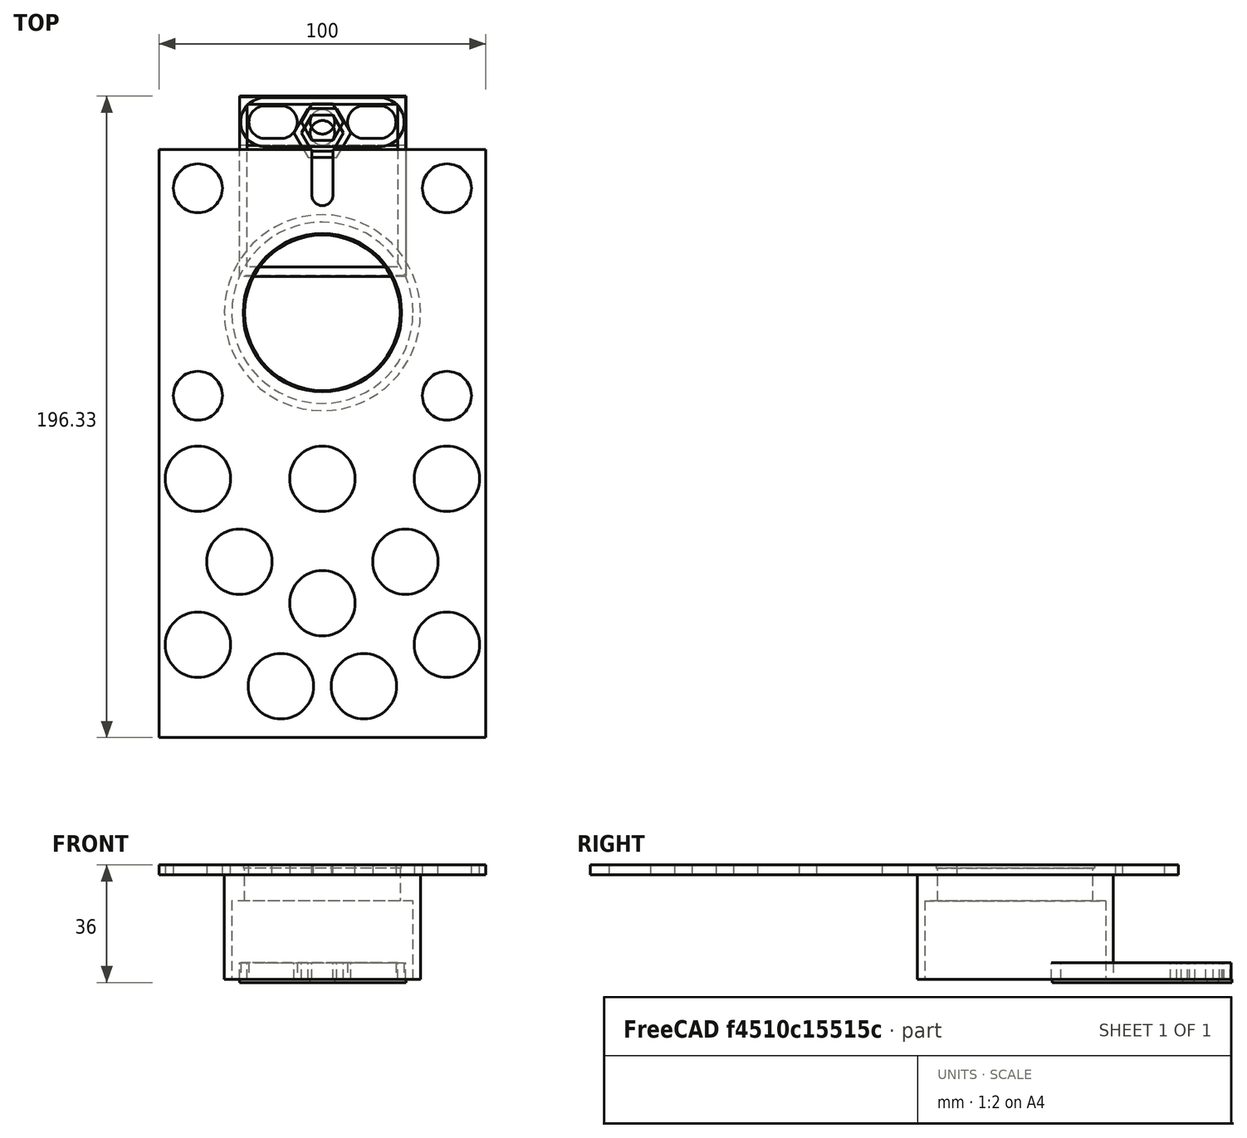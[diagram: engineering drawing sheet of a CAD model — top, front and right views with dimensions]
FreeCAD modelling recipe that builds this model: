
FCSTD DOCUMENT  (FreeCAD 0.19R24291 (Git))
Label: CellPhoneAdapter2in
License: All rights reserved
LicenseURL: http://en.wikipedia.org/wiki/All_rights_reserved
objects: TechDraw::DrawViewDimension×10, Sketcher::SketchObject×9, PartDesign::Pad×8, TechDraw::DrawProjGroupItem×4, PartDesign::Body×3, App::Part×3, PartDesign::Pocket×1, TechDraw::DrawSVGTemplate×1, TechDraw::DrawProjGroup×1, TechDraw::DrawPage×1
note: 30 computed .brp shape members not serialized (recipe doc carries the construction recipe); baked Part::Feature solids carry a one-line shape summary decoded from their .brp

FEATURE [Sketcher::SketchObject] Sketch  label="SketchTube"
  FullyConstrained = true
  MapMode = 5
  Support = -> [XY_Plane001]
  sketch-geometry (2):
    g0: Circle CenterX=0 CenterY=0 CenterZ=0 NormalX=0 NormalY=0 NormalZ=1 AngleXU=0 Radius=27.725
    g1: Circle CenterX=0 CenterY=0 CenterZ=0 NormalX=0 NormalY=0 NormalZ=1 AngleXU=0 Radius=30
  constraints (4):
    c: Coincident(g0,g-1)
    c: Coincident(g1,g-1)
    c: Diameter(g1) = 60
    c: Diameter(g0) = 55.45
FEATURE [PartDesign::Pad] Pad  label="PadTubeEyePiece"
  Direction = (1,1,1)
  Length = 32
  Length2 = 100
  Profile = -> Sketch
  Type = 0
FEATURE [Sketcher::SketchObject] Sketch001
  FullyConstrained = false
  MapMode = 5
  Placement = pos=(0,0,32) rot=(0,0,1;0rad)
  Support = -> [Pad]
  sketch-geometry (26):
    g0: LineSegment StartX=-100 StartY=50 StartZ=0 EndX=100 EndY=50 EndZ=0
    g1: ArcOfCircle CenterX=0 CenterY=36 CenterZ=0 NormalX=0 NormalY=0 NormalZ=1 AngleXU=0 Radius=3.2 StartAngle=3.14159 EndAngle=6.28319
    g2: ArcOfCircle CenterX=-1e-16 CenterY=106.723 CenterZ=0 NormalX=0 NormalY=0 NormalZ=1 AngleXU=0 Radius=3.2 StartAngle=0 EndAngle=3.14159
    g3: LineSegment StartX=3.2 StartY=36 StartZ=0 EndX=3.2 EndY=106.723 EndZ=0
    g4: LineSegment StartX=-3.2 StartY=36 StartZ=0 EndX=-3.2 EndY=106.723 EndZ=0
    g5: LineSegment StartX=3.2 StartY=50 StartZ=0 EndX=3.2 EndY=36 EndZ=0
    g6: LineSegment StartX=-3.2 StartY=50 StartZ=0 EndX=-50 EndY=50 EndZ=0
    g7: LineSegment StartX=-50 StartY=50 StartZ=0 EndX=-50 EndY=-130 EndZ=0
    g8: LineSegment StartX=-50 StartY=-130 StartZ=0 EndX=50 EndY=-130 EndZ=0
    g9: LineSegment StartX=50 StartY=-130 StartZ=0 EndX=50 EndY=50 EndZ=0
    g10: LineSegment StartX=50 StartY=50 StartZ=0 EndX=3.2 EndY=50 EndZ=0
    g11: LineSegment StartX=-3.2 StartY=50 StartZ=0 EndX=-3.2 EndY=36 EndZ=0
    g12: Circle CenterX=0 CenterY=-50.8 CenterZ=0 NormalX=0 NormalY=0 NormalZ=1 AngleXU=0 Radius=10
    g13: Circle CenterX=-38.1 CenterY=-50.8 CenterZ=0 NormalX=0 NormalY=0 NormalZ=1 AngleXU=0 Radius=10
    g14: Circle CenterX=38.1 CenterY=-50.8 CenterZ=0 NormalX=0 NormalY=0 NormalZ=1 AngleXU=0 Radius=10
    g15: Circle CenterX=-25.4 CenterY=-76.2 CenterZ=0 NormalX=0 NormalY=0 NormalZ=1 AngleXU=0 Radius=10
    g16: Circle CenterX=25.4 CenterY=-76.2 CenterZ=0 NormalX=0 NormalY=0 NormalZ=1 AngleXU=0 Radius=10
    g17: Circle CenterX=0 CenterY=-88.9 CenterZ=0 NormalX=0 NormalY=0 NormalZ=1 AngleXU=0 Radius=10
    g18: Circle CenterX=-38.1 CenterY=-101.6 CenterZ=0 NormalX=0 NormalY=0 NormalZ=1 AngleXU=0 Radius=10
    g19: Circle CenterX=38.1 CenterY=-101.6 CenterZ=0 NormalX=0 NormalY=0 NormalZ=1 AngleXU=0 Radius=10
    g20: Circle CenterX=-12.7 CenterY=-114.3 CenterZ=0 NormalX=0 NormalY=0 NormalZ=1 AngleXU=0 Radius=10
    g21: Circle CenterX=12.7 CenterY=-114.3 CenterZ=0 NormalX=0 NormalY=0 NormalZ=1 AngleXU=0 Radius=10
    g22: Circle CenterX=-38.1 CenterY=38.1 CenterZ=0 NormalX=0 NormalY=0 NormalZ=1 AngleXU=0 Radius=7.5
    g23: Circle CenterX=38.1 CenterY=38.1 CenterZ=0 NormalX=0 NormalY=0 NormalZ=1 AngleXU=0 Radius=7.5
    g24: Circle CenterX=38.1 CenterY=-25.4 CenterZ=0 NormalX=0 NormalY=0 NormalZ=1 AngleXU=0 Radius=7.5
    g25: Circle CenterX=-38.1 CenterY=-25.4 CenterZ=0 NormalX=0 NormalY=0 NormalZ=1 AngleXU=0 Radius=7.5
  constraints (47):
    c: Symmetric(g0,g0,g-2)
    c: DistanceY(g-1,g0) = 50
    c: Tangent(g1,g4) = 1.5708
    c: Tangent(g1,g3) = -1.5708
    c: Tangent(g3,g2) = -1.5708
    c: Tangent(g4,g2) = 1.5708
    c: Vertical(g3)
    c: Equal(g1,g2)
    c: PointOnObject(g1,g-2)
    c: DistanceX(g1,g1) = 6.4
    c: PointOnObject(g5,g0)
    c: Coincident(g5,g1)
    c: Vertical(g5)
    c: PointOnObject(g6,g4)
    c: PointOnObject(g6,g0)
    c: PointOnObject(g6,g0)
    c: Coincident(g6,g7)
    c: Vertical(g7)
    c: Coincident(g7,g8)
    c: Coincident(g8,g9)
    c: PointOnObject(g9,g0)
    c: Vertical(g9)
    c: Coincident(g9,g10)
    c: Coincident(g10,g5)
    c: Symmetric(g7,g8,g-2)
    c: DistanceX(g7,g8) = 100
    c: DistanceY(g7,g6) = 180
    c: DistanceY(g-1,g1) = 36
    c: DistanceX(g0,g0) = 200
    c: Coincident(g6,g11)
    c: Coincident(g11,g1)
    c: PointOnObject(g12,g-2)
    c: PointOnObject(g17,g-2)
    c: Diameter(g13) = 20
    c: Equal(g14,g13)
    c: Equal(g13,g15)
    c: Equal(g15,g16)
    c: Equal(g16,g18)
    c: Equal(g18,g19)
    c: Equal(g19,g17)
    c: Equal(g12,g13)
    c: Equal(g13,g20)
    c: Equal(g20,g21)
    c: Diameter(g22) = 15
    c: Equal(g22,g23)
    c: Equal(g23,g24)
    c: Equal(g24,g25)
FEATURE [PartDesign::Pad] Pad001  label="PadPlatform"
  BaseFeature = -> Pad
  Direction = (1,1,1)
  Length = 3
  Length2 = 100
  Profile = -> Sketch001
  Type = 0
FEATURE [Sketcher::SketchObject] Sketch002
  FullyConstrained = true
  MapMode = 5
  Support = -> [XY_Plane001]
  sketch-geometry (1):
    g0: Circle CenterX=0 CenterY=0 CenterZ=0 NormalX=0 NormalY=0 NormalZ=1 AngleXU=0 Radius=24.25
  constraints (2):
    c: Coincident(g0,g-1)
    c: Diameter(g0) = 48.5
FEATURE [PartDesign::Pocket] Pocket  label="PocketEyePieceOuter"
  BaseFeature = -> Pad001
  Length = 5
  Length2 = 100
  Profile = -> Sketch002
  Reversed = true
  Type = 1
FEATURE [TechDraw::DrawSVGTemplate] Template
  Height = 304.8
  Orientation = 1
  Width = 457.2
FEATURE [Sketcher::SketchObject] Sketch003
  AttachmentOffset = pos=(0,0,34) rot=(0,0,1;0rad)
  FullyConstrained = true
  MapMode = 5
  Placement = pos=(0,0,34) rot=(0,0,1;0rad)
  Support = -> [XY_Plane001]
  sketch-geometry (2):
    g0: Circle CenterX=0 CenterY=0 CenterZ=0 NormalX=0 NormalY=0 NormalZ=1 AngleXU=0 Radius=23.79
    g1: Circle CenterX=0 CenterY=0 CenterZ=0 NormalX=0 NormalY=0 NormalZ=1 AngleXU=0 Radius=30
  constraints (4):
    c: Coincident(g0,g-1)
    c: Coincident(g1,g0)
    c: Diameter(g0) = 47.58
    c: Diameter(g1) = 60
FEATURE [PartDesign::Pad] Pad002  label="PadRuberCupGrab"
  BaseFeature = -> Pocket
  Direction = (1,1,1)
  Length = 10
  Length2 = 100
  Profile = -> Sketch003
  Reversed = true
  Type = 0
FEATURE [PartDesign::Body] Body  label="BodyEyePiecePlatform"
  Group = -> [Sketch,Pad,Sketch001,Pad001,Sketch002,Pocket,Sketch003,Pad002]
  Origin = -> Origin001
  Tip = -> Pad002
FEATURE [App::Part] Part
  Group = -> [Body]
  Origin = -> Origin
FEATURE [TechDraw::DrawProjGroupItem] ProjItem  label="Front"
  CoarseView = false
  Direction = (0,0,1)
  Focus = 100
  HardHidden = false
  IsoCount = 0
  IsoHidden = false
  IsoVisible = false
  LockPosition = true
  Perspective = false
  Rotation = 0
  RotationVector = (1,0,0)
  ScaleType = 2
  SeamHidden = false
  SeamVisible = true
  SmoothHidden = false
  SmoothVisible = true
  Source = -> [Body]
  Type = 0
  X = 0
  XDirection = (1,0,0)
  Y = 0
FEATURE [TechDraw::DrawProjGroupItem] ProjItem001  label="Left"
  CoarseView = false
  Direction = (-1,0,1e-16)
  Focus = 100
  HardHidden = false
  IsoCount = 0
  IsoHidden = false
  IsoVisible = false
  LockPosition = true
  Perspective = false
  Rotation = 0
  RotationVector = (1,0,0)
  ScaleType = 2
  SeamHidden = false
  SeamVisible = true
  SmoothHidden = false
  SmoothVisible = true
  Source = -> [Body]
  Type = 1
  X = 191.563
  XDirection = (1e-16,0,1)
  Y = 0
FEATURE [TechDraw::DrawViewDimension] Dimension
  Arbitrary = false
  ArbitraryTolerances = false
  EqualTolerance = true
  FormatSpec = ⌀%.3f
  FormatSpecOverTolerance = %+.3f
  FormatSpecUnderTolerance = %+.3f
  Inverted = false
  LockPosition = false
  MeasureType = 1
  OverTolerance = 0
  References2D = -> [ProjItem]
  Rotation = 0
  ScaleType = 2
  TheoreticalExact = false
  Type = 5
  UnderTolerance = 0
  X = 29.9267
  Y = 72.869
FEATURE [TechDraw::DrawViewDimension] Dimension001
  Arbitrary = false
  ArbitraryTolerances = false
  EqualTolerance = true
  FormatSpec = %.3f
  FormatSpecOverTolerance = %+.3f
  FormatSpecUnderTolerance = %+.3f
  Inverted = false
  LockPosition = false
  MeasureType = 1
  OverTolerance = 0
  References2D = -> [ProjItem001]
  Rotation = 0
  ScaleType = 2
  TheoreticalExact = false
  Type = 2
  UnderTolerance = 0
  X = -32.9374
  Y = 32.5065
FEATURE [TechDraw::DrawViewDimension] Dimension002
  Arbitrary = false
  ArbitraryTolerances = false
  EqualTolerance = true
  FormatSpec = %.3f
  FormatSpecOverTolerance = %+.3f
  FormatSpecUnderTolerance = %+.3f
  Inverted = false
  LockPosition = false
  MeasureType = 1
  OverTolerance = 0
  References2D = -> [ProjItem001]
  Rotation = 0
  ScaleType = 2
  TheoreticalExact = false
  Type = 1
  UnderTolerance = 0
  X = 0.993457
  Y = 98.2855
FEATURE [TechDraw::DrawViewDimension] Dimension003
  Arbitrary = false
  ArbitraryTolerances = false
  EqualTolerance = true
  FormatSpec = %.3f
  FormatSpecOverTolerance = %+.3f
  FormatSpecUnderTolerance = %+.3f
  Inverted = false
  LockPosition = false
  MeasureType = 1
  OverTolerance = 0
  References2D = -> [ProjItem001]
  Rotation = 0
  ScaleType = 2
  TheoreticalExact = false
  Type = 1
  UnderTolerance = 0
  X = 26.538
  Y = -79.7421
FEATURE [TechDraw::DrawViewDimension] Dimension004
  Arbitrary = false
  ArbitraryTolerances = false
  EqualTolerance = true
  FormatSpec = %.3f
  FormatSpecOverTolerance = %+.3f
  FormatSpecUnderTolerance = %+.3f
  Inverted = false
  LockPosition = false
  MeasureType = 1
  OverTolerance = 0
  References2D = -> [ProjItem]
  Rotation = 0
  ScaleType = 2
  TheoreticalExact = false
  Type = 1
  UnderTolerance = 0
  X = 2.82767
  Y = -101.939
FEATURE [TechDraw::DrawViewDimension] Dimension005
  Arbitrary = false
  ArbitraryTolerances = false
  EqualTolerance = true
  FormatSpec = %.3f
  FormatSpecOverTolerance = %+.3f
  FormatSpecUnderTolerance = %+.3f
  Inverted = false
  LockPosition = false
  MeasureType = 1
  OverTolerance = 0
  References2D = -> [ProjItem]
  Rotation = 0
  ScaleType = 2
  TheoreticalExact = false
  Type = 2
  UnderTolerance = 0
  X = -65.6192
  Y = -0.628372
FEATURE [TechDraw::DrawViewDimension] Dimension006
  Arbitrary = false
  ArbitraryTolerances = false
  EqualTolerance = true
  FormatSpec = %.3f
  FormatSpecOverTolerance = %+.3f
  FormatSpecUnderTolerance = %+.3f
  Inverted = false
  LockPosition = false
  MeasureType = 1
  OverTolerance = 0
  References2D = -> [ProjItem]
  Rotation = 0
  ScaleType = 2
  TheoreticalExact = false
  Type = 2
  UnderTolerance = 0
  X = -21.3391
  Y = 107.15
FEATURE [TechDraw::DrawViewDimension] Dimension007
  Arbitrary = false
  ArbitraryTolerances = false
  EqualTolerance = true
  FormatSpec = %.3f
  FormatSpecOverTolerance = %+.3f
  FormatSpecUnderTolerance = %+.3f
  Inverted = false
  LockPosition = false
  MeasureType = 1
  OverTolerance = 0
  References2D = -> [ProjItem]
  Rotation = 0
  ScaleType = 2
  TheoreticalExact = false
  Type = 1
  UnderTolerance = 0
  X = 12.2183
  Y = 102.873
FEATURE [TechDraw::DrawViewDimension] Dimension008
  Arbitrary = false
  ArbitraryTolerances = false
  EqualTolerance = true
  FormatSpec = ⌀%.3f
  FormatSpecOverTolerance = %+.3f
  FormatSpecUnderTolerance = %+.3f
  Inverted = false
  LockPosition = false
  MeasureType = 1
  OverTolerance = 0
  References2D = -> [ProjItem]
  Rotation = 0
  ScaleType = 2
  TheoreticalExact = false
  Type = 5
  UnderTolerance = 0
  X = 32.2663
  Y = 59.354
FEATURE [TechDraw::DrawProjGroupItem] ProjItem003  label="FrontTopRight"
  CoarseView = false
  Direction = (0.57735,0.57735,0.57735)
  Focus = 100
  HardHidden = false
  IsoCount = 0
  IsoHidden = false
  IsoVisible = false
  LockPosition = true
  Perspective = false
  Rotation = 0
  RotationVector = (1,0,0)
  ScaleType = 2
  SeamHidden = false
  SeamVisible = true
  SmoothHidden = false
  SmoothVisible = true
  Source = -> [Body]
  Type = 7
  X = 316.549
  XDirection = (0.707107,0,-0.707107)
  Y = 26.588
FEATURE [TechDraw::DrawProjGroupItem] ProjItem004  label="Rear"
  CoarseView = false
  Direction = (0,0,-1)
  Focus = 100
  HardHidden = false
  IsoCount = 0
  IsoHidden = false
  IsoVisible = false
  LockPosition = true
  Perspective = false
  Rotation = 0
  RotationVector = (1,0,0)
  ScaleType = 2
  SeamHidden = false
  SeamVisible = true
  SmoothHidden = false
  SmoothVisible = true
  Source = -> [Body]
  Type = 3
  X = 109.194
  XDirection = (-1,0,0)
  Y = 0
FEATURE [TechDraw::DrawProjGroup] ProjGroup
  Anchor = -> ProjItem
  AutoDistribute = false
  LockPosition = false
  ProjectionType = 0
  Rotation = 0
  ScaleType = 2
  Source = -> [Body]
  Views = -> [ProjItem,ProjItem001,ProjItem003,ProjItem004]
  X = 76.8505
  Y = 167.106
  spacingX = 15
  spacingY = 15
FEATURE [TechDraw::DrawViewDimension] Dimension009
  Arbitrary = false
  ArbitraryTolerances = false
  EqualTolerance = true
  FormatSpec = %.3f
  FormatSpecOverTolerance = %+.3f
  FormatSpecUnderTolerance = %+.3f
  Inverted = false
  LockPosition = false
  MeasureType = 1
  OverTolerance = 0
  References2D = -> [ProjItem]
  Rotation = 0
  ScaleType = 2
  TheoreticalExact = false
  Type = 2
  UnderTolerance = 0
  X = -37.103
  Y = 51.49
FEATURE [TechDraw::DrawPage] Page  label="Page11x17"
  KeepUpdated = true
  NextBalloonIndex = 1
  ProjectionType = 0
  Template = -> Template
  Views = -> [ProjGroup,Dimension,Dimension001,Dimension002,Dimension003,Dimension004,Dimension005,Dimension006,Dimension007,Dimension008,Dimension009]
FEATURE [Sketcher::SketchObject] Sketch004
  FullyConstrained = false
  MapMode = 5
  Support = -> [XY_Plane003]
  sketch-geometry (19):
    g0: ArcOfCircle CenterX=-17.5 CenterY=58.3385 CenterZ=0 NormalX=0 NormalY=0 NormalZ=1 AngleXU=0 Radius=7.5 StartAngle=1.5708 EndAngle=4.71239
    g1: ArcOfCircle CenterX=17.5 CenterY=58.3385 CenterZ=0 NormalX=0 NormalY=0 NormalZ=1 AngleXU=0 Radius=7.5 StartAngle=4.71239 EndAngle=7.85398
    g2: LineSegment StartX=-17.5 StartY=50.8385 StartZ=0 EndX=17.5 EndY=50.8385 EndZ=0
    g3: LineSegment StartX=-17.5 StartY=65.8385 StartZ=0 EndX=17.5 EndY=65.8385 EndZ=0
    g4: LineSegment StartX=3.20429 StartY=52.7885 StartZ=0 EndX=6.40859 EndY=58.3385 EndZ=0
    g5: LineSegment StartX=6.40859 StartY=58.3385 StartZ=0 EndX=3.20429 EndY=63.8885 EndZ=0
    g6: LineSegment StartX=3.20429 StartY=63.8885 StartZ=0 EndX=-3.20429 EndY=63.8885 EndZ=0
    g7: LineSegment StartX=-3.20429 StartY=63.8885 StartZ=0 EndX=-6.40859 EndY=58.3385 EndZ=0
    g8: LineSegment StartX=-6.40859 StartY=58.3385 StartZ=0 EndX=-3.20429 EndY=52.7885 EndZ=0
    g9: LineSegment StartX=-3.20429 StartY=52.7885 StartZ=0 EndX=3.20429 EndY=52.7885 EndZ=0
    g10: Circle CenterX=0 CenterY=58.3385 CenterZ=0 NormalX=0 NormalY=0 NormalZ=1 AngleXU=0 Radius=6.40859
    g11: ArcOfCircle CenterX=-17.5 CenterY=58.3385 CenterZ=0 NormalX=0 NormalY=0 NormalZ=1 AngleXU=0 Radius=5 StartAngle=1.5708 EndAngle=4.71239
    g12: ArcOfCircle CenterX=-12.7014 CenterY=58.3385 CenterZ=0 NormalX=0 NormalY=0 NormalZ=1 AngleXU=0 Radius=5 StartAngle=4.71239 EndAngle=7.85398
    g13: LineSegment StartX=-17.5 StartY=53.3385 StartZ=0 EndX=-12.7014 EndY=53.3385 EndZ=0
    g14: LineSegment StartX=-17.5 StartY=63.3385 StartZ=0 EndX=-12.7014 EndY=63.3385 EndZ=0
    g15: ArcOfCircle CenterX=17.5 CenterY=58.3385 CenterZ=0 NormalX=0 NormalY=0 NormalZ=1 AngleXU=0 Radius=5 StartAngle=4.71239 EndAngle=7.85398
    g16: ArcOfCircle CenterX=12.7014 CenterY=58.3385 CenterZ=0 NormalX=0 NormalY=0 NormalZ=1 AngleXU=0 Radius=5 StartAngle=1.5708 EndAngle=4.71239
    g17: LineSegment StartX=17.5 StartY=63.3385 StartZ=0 EndX=12.7014 EndY=63.3385 EndZ=0
    g18: LineSegment StartX=17.5 StartY=53.3385 StartZ=0 EndX=12.7014 EndY=53.3385 EndZ=0
  constraints (41):
    c: Tangent(g0,g3) = 1.5708
    c: Tangent(g0,g2) = -1.5708
    c: Tangent(g2,g1) = -1.5708
    c: Tangent(g3,g1) = 1.5708
    c: Equal(g0,g1)
    c: Coincident(g4,g5)
    c: Coincident(g5,g6)
    c: Coincident(g6,g7)
    c: Coincident(g7,g8)
    c: Coincident(g8,g9)
    c: Coincident(g9,g4)
    c: Equal(g4, g5-g9) x5
    c: PointOnObject(g4,g10)
    c: PointOnObject(g5,g10)
    c: PointOnObject(g6,g10)
    c: PointOnObject(g7,g10)
    c: PointOnObject(g8,g10)
    c: PointOnObject(g9,g10)
    c: PointOnObject(g10,g-2)
    c: Horizontal(g6)
    c: DistanceY(g4,g5) = 11.1
    c: DistanceY(g0,g0) = 15
    c: DistanceX(g0,g1) = 35
    c: Horizontal(g1,g10)
    c: Symmetric(g1,g0,g-2)
    c: Tangent(g11,g14) = 1.5708
    c: Tangent(g11,g13) = -1.5708
    c: Tangent(g13,g12) = -1.5708
    c: Tangent(g14,g12) = 1.5708
    c: Horizontal(g13)
    c: Equal(g11,g12)
    c: Coincident(g11,g0)
    c: Tangent(g15,g18) = 1.5708
    c: Tangent(g15,g17) = -1.5708
    c: Tangent(g17,g16) = -1.5708
    c: Tangent(g18,g16) = 1.5708
    c: Horizontal(g17)
    c: Equal(g15,g16)
    c: Coincident(g15,g1)
    c: DistanceY(g12,g12) = 10
    c: DistanceY(g16,g16) = 10
FEATURE [PartDesign::Pad] Pad003  label="PadHexAndOvels"
  Direction = (1,1,1)
  Length = 5
  Length2 = 100
  Profile = -> Sketch004
  Type = 0
FEATURE [Sketcher::SketchObject] Sketch005
  FullyConstrained = false
  MapMode = 5
  Support = -> [XY_Plane003]
  sketch-geometry (5):
    g0: LineSegment StartX=25.4 StartY=51.2097 StartZ=0 EndX=-25.4 EndY=51.2097 EndZ=0
    g1: LineSegment StartX=-25.4 StartY=51.2097 StartZ=0 EndX=-25.4 EndY=66.2097 EndZ=0
    g2: LineSegment StartX=-25.4 StartY=66.2097 StartZ=0 EndX=25.4 EndY=66.2097 EndZ=0
    g3: LineSegment StartX=25.4 StartY=66.2097 StartZ=0 EndX=25.4 EndY=51.2097 EndZ=0
    g4: Circle CenterX=0 CenterY=58.4595 CenterZ=0 NormalX=0 NormalY=0 NormalZ=1 AngleXU=0 Radius=3.75
  constraints (11):
    c: Coincident(g0,g1)
    c: Coincident(g1,g2)
    c: Coincident(g2,g3)
    c: Coincident(g3,g0)
    c: Horizontal(g0)
    c: Horizontal(g2)
    c: Vertical(g1)
    c: Vertical(g3)
    c: DistanceY(g1,g1) = 15
    c: PointOnObject(g4,g-2)
    c: Diameter(g4) = 7.5
FEATURE [PartDesign::Pad] Pad004  label="PadBase"
  BaseFeature = -> Pad003
  Direction = (1,1,1)
  Length = 1
  Length2 = 100
  Profile = -> Sketch005
  Reversed = true
  Type = 0
FEATURE [PartDesign::Body] Body001  label="BodyLocator1"
  Group = -> [Sketch004,Pad003,Sketch005,Pad004]
  Origin = -> Origin003
  Tip = -> Pad004
FEATURE [App::Part] Part001  label="PartLocator1"
  Group = -> [Body001]
  Origin = -> Origin002
  Placement = pos=(-119,-49,0) rot=(0,0,1;4.71239rad)
FEATURE [Sketcher::SketchObject] Sketch006
  FullyConstrained = false
  MapMode = 5
  Support = -> [XY_Plane004]
  expr: Constraints[20] = Sketch007.Constraints[10]
  sketch-geometry (16):
    g0: LineSegment StartX=3.20429 StartY=49.45 StartZ=0 EndX=6.40859 EndY=55 EndZ=0
    g1: LineSegment StartX=6.40859 StartY=55 StartZ=0 EndX=3.20429 EndY=60.55 EndZ=0
    g2: LineSegment StartX=3.20429 StartY=60.55 StartZ=0 EndX=-3.20429 EndY=60.55 EndZ=0
    g3: LineSegment StartX=-3.20429 StartY=60.55 StartZ=0 EndX=-6.40859 EndY=55 EndZ=0
    g4: LineSegment StartX=-6.40859 StartY=55 StartZ=0 EndX=-3.20429 EndY=49.45 EndZ=0
    g5: LineSegment StartX=-3.20429 StartY=49.45 StartZ=0 EndX=3.20429 EndY=49.45 EndZ=0
    g6: Circle CenterX=0 CenterY=55 CenterZ=0 NormalX=0 NormalY=0 NormalZ=1 AngleXU=0 Radius=6.40859
    g7: Circle CenterX=0 CenterY=55 CenterZ=0 NormalX=0 NormalY=0 NormalZ=1 AngleXU=0 Radius=3.75
    g8: GeomPoint X=0 Y=55 Z=0
    g9: LineSegment StartX=4.33013 StartY=47.5 StartZ=0 EndX=8.66025 EndY=55 EndZ=0
    g10: LineSegment StartX=8.66025 StartY=55 StartZ=0 EndX=4.33013 EndY=62.5 EndZ=0
    g11: LineSegment StartX=4.33013 StartY=62.5 StartZ=0 EndX=-4.33013 EndY=62.5 EndZ=0
    g12: LineSegment StartX=-4.33013 StartY=62.5 StartZ=0 EndX=-8.66025 EndY=55 EndZ=0
    g13: LineSegment StartX=-8.66025 StartY=55 StartZ=0 EndX=-4.33013 EndY=47.5 EndZ=0
    g14: LineSegment StartX=-4.33013 StartY=47.5 StartZ=0 EndX=4.33013 EndY=47.5 EndZ=0
    g15: Circle CenterX=0 CenterY=55 CenterZ=0 NormalX=0 NormalY=0 NormalZ=1 AngleXU=0 Radius=8.66025
  constraints (35):
    c: Coincident(g0,g1)
    c: Coincident(g1,g2)
    c: Coincident(g2,g3)
    c: Coincident(g3,g4)
    c: Coincident(g4,g5)
    c: Coincident(g5,g0)
    c: Equal(g0, g1-g5) x5
    c: PointOnObject(g0,g6)
    c: PointOnObject(g1,g6)
    c: PointOnObject(g2,g6)
    c: PointOnObject(g3,g6)
    c: PointOnObject(g4,g6)
    c: PointOnObject(g5,g6)
    c: PointOnObject(g6,g-2)
    c: Horizontal(g2)
    c: DistanceY(g0,g1) = 11.1
    c: Diameter(g7) = 7.5
    c: Coincident(g7,g8)
    c: Coincident(g6,g7)
    c: Coincident(g9,g10)
    c: Coincident(g10,g11)
    c: Coincident(g11,g12)
    c: Coincident(g12,g13)
    c: Coincident(g13,g14)
    c: Coincident(g14,g9)
    c: Equal(g9, g10-g14) x5
    c: PointOnObject(g9,g15)
    c: PointOnObject(g10,g15)
    c: PointOnObject(g11,g15)
    c: PointOnObject(g12,g15)
    c: PointOnObject(g13,g15)
    c: PointOnObject(g14,g15)
    c: Coincident(g15,g6)
    c: Horizontal(g11)
    c: DistanceY(g13,g11) = 15
FEATURE [PartDesign::Pad] Pad005  label="PadHexAndOvels001"
  Direction = (1,1,1)
  Length = 5
  Length2 = 100
  Profile = -> Sketch006
  Type = 0
FEATURE [Sketcher::SketchObject] Sketch007
  FullyConstrained = false
  MapMode = 5
  Support = -> [XY_Plane004]
  sketch-geometry (10):
    g0: LineSegment StartX=25.555 StartY=11.3284 StartZ=0 EndX=-25.4 EndY=11.3284 EndZ=0
    g1: LineSegment StartX=-25.4 StartY=11.3284 StartZ=0 EndX=-25.4 EndY=66.3284 EndZ=0
    g2: LineSegment StartX=-25.4 StartY=66.3284 StartZ=0 EndX=25.555 EndY=66.3284 EndZ=0
    g3: LineSegment StartX=25.555 StartY=66.3284 StartZ=0 EndX=25.555 EndY=11.3284 EndZ=0
    g4: Circle CenterX=0 CenterY=55.079 CenterZ=0 NormalX=0 NormalY=0 NormalZ=1 AngleXU=0 Radius=3.75
    g5: LineSegment StartX=-20 StartY=60 StartZ=0 EndX=20 EndY=60 EndZ=0
    g6: LineSegment StartX=-20 StartY=50.1482 StartZ=0 EndX=20.0394 EndY=50.1482 EndZ=0
    g7: LineSegment StartX=-20 StartY=60 StartZ=0 EndX=20.0394 EndY=50.1482 EndZ=0
    g8: LineSegment StartX=-20 StartY=50.1482 StartZ=0 EndX=20 EndY=60 EndZ=0
    g9: GeomPoint X=0 Y=55.079 Z=0
  constraints (19):
    c: Coincident(g0,g1)
    c: Coincident(g1,g2)
    c: Coincident(g2,g3)
    c: Coincident(g3,g0)
    c: Horizontal(g0)
    c: Horizontal(g2)
    c: Vertical(g1)
    c: Vertical(g3)
    c: DistanceY(g1,g1) = 55
    c: PointOnObject(g4,g-2)
    c: Diameter(g4) = 7.5
    c: Horizontal(g5)
    c: Horizontal(g6)
    c: Coincident(g7,g5)
    c: Coincident(g7,g6)
    c: Coincident(g8,g6)
    c: PointOnObject(g9,g7)
    c: Coincident(g4,g9)
    c: Coincident(g5,g8)
FEATURE [PartDesign::Pad] Pad006  label="PadBase001"
  BaseFeature = -> Pad005
  Direction = (1,1,1)
  Length = 1
  Length2 = 100
  Profile = -> Sketch007
  Reversed = true
  Type = 0
FEATURE [Sketcher::SketchObject] Sketch008
  FullyConstrained = false
  MapMode = 5
  Support = -> [XY_Plane004]
  sketch-geometry (8):
    g0: LineSegment StartX=-25.4 StartY=66.1135 StartZ=0 EndX=25.4 EndY=66.1135 EndZ=0
    g1: LineSegment StartX=25.4 StartY=66.1135 StartZ=0 EndX=25.4 EndY=11.1135 EndZ=0
    g2: LineSegment StartX=25.4 StartY=11.1135 StartZ=0 EndX=-25.4 EndY=11.1135 EndZ=0
    g3: LineSegment StartX=-25.4 StartY=11.1135 StartZ=0 EndX=-25.4 EndY=66.1135 EndZ=0
    g4: LineSegment StartX=-23 StartY=63.8001 StartZ=0 EndX=23 EndY=63.8001 EndZ=0
    g5: LineSegment StartX=23 StartY=63.8001 StartZ=0 EndX=23 EndY=13.9674 EndZ=0
    g6: LineSegment StartX=23 StartY=13.9674 StartZ=0 EndX=-23 EndY=13.9674 EndZ=0
    g7: LineSegment StartX=-23 StartY=13.9674 StartZ=0 EndX=-23 EndY=63.8001 EndZ=0
  constraints (19):
    c: Coincident(g0,g1)
    c: Coincident(g1,g2)
    c: Coincident(g2,g3)
    c: Coincident(g3,g0)
    c: Horizontal(g0)
    c: Vertical(g1)
    c: Vertical(g3)
    c: DistanceY(g3,g3) = 55
    c: DistanceX(g0,g0) = 50.8
    c: Symmetric(g2,g1,g-2)
    c: Coincident(g4,g5)
    c: Coincident(g5,g6)
    c: Coincident(g6,g7)
    c: Coincident(g7,g4)
    c: Horizontal(g4)
    c: Vertical(g5)
    c: Vertical(g7)
    c: Symmetric(g6,g5,g-2)
    c: DistanceX(g4,g4) = 46
FEATURE [PartDesign::Pad] Pad007  label="PadPerimiter"
  BaseFeature = -> Pad006
  Direction = (1,1,1)
  Length = 5
  Length2 = 100
  Profile = -> Sketch008
  Type = 0
FEATURE [PartDesign::Body] Body002  label="BodyLocatorBig"
  Group = -> [Sketch006,Pad005,Sketch007,Pad006,Sketch008,Pad007]
  Origin = -> Origin005
  Tip = -> Pad007
FEATURE [App::Part] Part002  label="PartLocatorBig"
  Group = -> [Body002]
  Origin = -> Origin004
